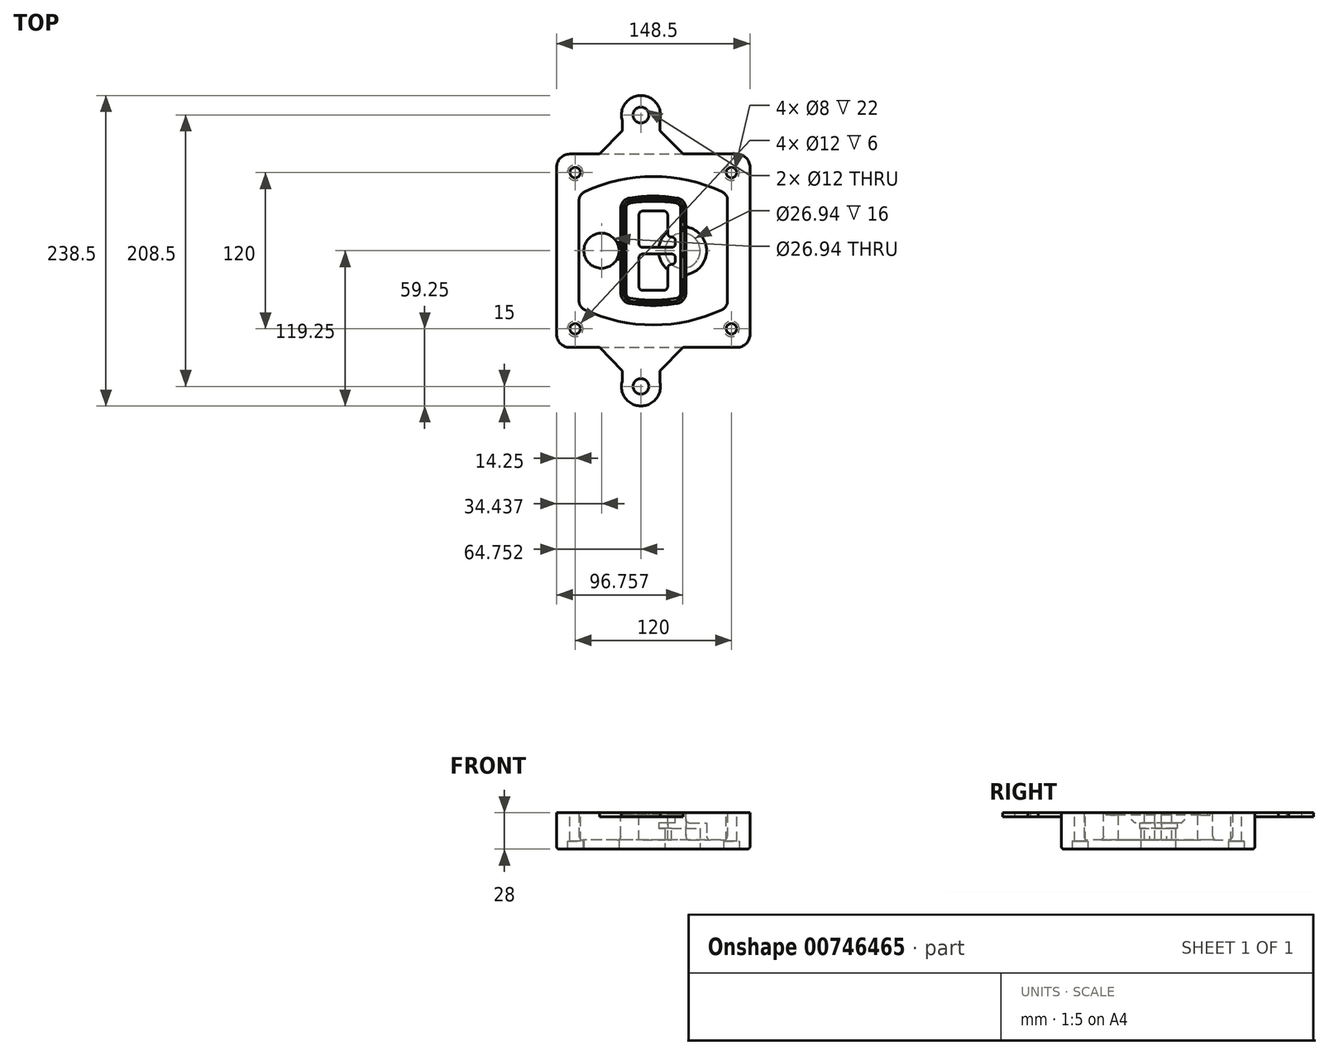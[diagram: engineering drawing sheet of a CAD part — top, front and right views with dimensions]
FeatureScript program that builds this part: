
annotation { "Feature Type Name" : "Feature", "Feature Type Description" : "" }
export const myFeature = defineFeature(function(context is Context, id is Id, definition is map)
    precondition{}
    {
        {
            var Q0;
            Q0=qCreatedBy(makeId("Top.planeOp"),FACE);
            var sketch = newSketch(context, id + "F0", { "sketchPlane" : qUnion([Q0])});
            skPoint(sketch, "E0.rect.middle", {"position": v(0, 0) * mm});
            skLineSegment(sketch, "E1.bottom", {"start": v(-64.25, -74.25) * mm, "end": v(64.25, -74.25) * mm});
            skLineSegment(sketch, "E1.top", {"start": v(-64.25, 74.25) * mm, "end": v(64.25, 74.25) * mm});
            skLineSegment(sketch, "E1.left", {"start": v(-74.25, -64.25) * mm, "end": v(-74.25, 64.25) * mm});
            skLineSegment(sketch, "E1.right", {"start": v(74.25, -64.25) * mm, "end": v(74.25, 64.25) * mm});
            skLineSegment(sketch, "E2", {"start": v(-74.25, 74.25) * mm, "end": v(74.25, -74.25) * mm, "construction": true});
            skLineSegment(sketch, "E3", {"start": v(74.25, 74.25) * mm, "end": v(-74.25, -74.25) * mm, "construction": true});
            skCircle(sketch, "E4", {"center": v(-60, 60) * mm, "radius": 4 * mm});
            skCircle(sketch, "E5", {"center": v(60, 60) * mm, "radius": 4 * mm});
            skCircle(sketch, "E6", {"center": v(60, -60) * mm, "radius": 4 * mm});
            skCircle(sketch, "E7", {"center": v(-60, -60) * mm, "radius": 4 * mm});
            skLineSegment(sketch, "E8", {"start": v(-60, 60) * mm, "end": v(60, 60) * mm, "construction": true});
            skLineSegment(sketch, "E9", {"start": v(60, 60) * mm, "end": v(60, -60) * mm, "construction": true});
            skLineSegment(sketch, "E10", {"start": v(60, -60) * mm, "end": v(-60, -60) * mm, "construction": true});
            skLineSegment(sketch, "E11", {"start": v(-60, -60) * mm, "end": v(-60, 60) * mm, "construction": true});
            skLineSegment(sketch, "E12", {"start": v(-60, 38.83) * mm, "end": v(-60, -38.83) * mm});
            skLineSegment(sketch, "E13", {"start": v(60, 38.83) * mm, "end": v(60, -38.83) * mm});
            skArc(sketch, "E14", {"start": v(54.26, 47.88) * mm, "mid": v(0, 60) * mm, "end": v(-54.26, 47.88) * mm});
            skArc(sketch, "E15", {"start": v(-54.26, -47.88) * mm, "mid": v(0, -60) * mm, "end": v(54.26, -47.88) * mm});
            skLineSegment(sketch, "E16", {"start": v(-60, 0) * mm, "end": v(60, 0) * mm, "construction": true});
            skPoint(sketch, "E17.visualSharp", {"position": v(-60, -45) * mm});
            skArc(sketch, "E17.filletArc", {"start": v(-60, -38.83) * mm, "mid": v(-58.44, -44.2) * mm, "end": v(-54.26, -47.88) * mm});
            skPoint(sketch, "E18.visualSharp", {"position": v(-60, 45) * mm});
            skArc(sketch, "E18.filletArc", {"start": v(-54.26, 47.88) * mm, "mid": v(-58.44, 44.2) * mm, "end": v(-60, 38.83) * mm});
            skPoint(sketch, "E19.visualSharp", {"position": v(60, 45) * mm});
            skArc(sketch, "E19.filletArc", {"start": v(60, 38.83) * mm, "mid": v(58.44, 44.2) * mm, "end": v(54.26, 47.88) * mm});
            skPoint(sketch, "E20.visualSharp", {"position": v(60, -45) * mm});
            skArc(sketch, "E20.filletArc", {"start": v(54.26, -47.88) * mm, "mid": v(58.44, -44.2) * mm, "end": v(60, -38.83) * mm});
            skPoint(sketch, "E21.visualSharp", {"position": v(-74.25, 74.25) * mm});
            skArc(sketch, "E21.filletArc", {"start": v(-64.25, 74.25) * mm, "mid": v(-71.32, 71.32) * mm, "end": v(-74.25, 64.25) * mm});
            skPoint(sketch, "E22.visualSharp", {"position": v(74.25, 74.25) * mm});
            skArc(sketch, "E22.filletArc", {"start": v(74.25, 64.25) * mm, "mid": v(71.32, 71.32) * mm, "end": v(64.25, 74.25) * mm});
            skPoint(sketch, "E23.visualSharp", {"position": v(74.25, -74.25) * mm});
            skArc(sketch, "E23.filletArc", {"start": v(64.25, -74.25) * mm, "mid": v(71.32, -71.32) * mm, "end": v(74.25, -64.25) * mm});
            skPoint(sketch, "E24.visualSharp", {"position": v(-74.25, -74.25) * mm});
            skArc(sketch, "E24.filletArc", {"start": v(-74.25, -64.25) * mm, "mid": v(-71.32, -71.32) * mm, "end": v(-64.25, -74.25) * mm});
            skArc(sketch, "E25.0", {"start": v(57, 38.83) * mm, "mid": v(55.9, 42.58) * mm, "end": v(52.98, 45.17) * mm});
            skLineSegment(sketch, "E25.1", {"start": v(57, 38.83) * mm, "end": v(57, -38.83) * mm});
            skArc(sketch, "E25.2", {"start": v(52.98, -45.17) * mm, "mid": v(55.9, -42.58) * mm, "end": v(57, -38.83) * mm});
            skArc(sketch, "E25.3", {"start": v(-52.98, -45.17) * mm, "mid": v(0, -57) * mm, "end": v(52.98, -45.17) * mm});
            skArc(sketch, "E25.4", {"start": v(-57, -38.83) * mm, "mid": v(-55.9, -42.58) * mm, "end": v(-52.98, -45.17) * mm});
            skArc(sketch, "E25.5", {"start": v(52.98, 45.17) * mm, "mid": v(0, 57) * mm, "end": v(-52.98, 45.17) * mm});
            skLineSegment(sketch, "E25.6", {"start": v(-57, 38.83) * mm, "end": v(-57, -38.83) * mm});
            skArc(sketch, "E25.7", {"start": v(-52.98, 45.17) * mm, "mid": v(-55.9, 42.58) * mm, "end": v(-57, 38.83) * mm});
            skArc(sketch, "E26.0", {"start": v(-55.96, 51.5) * mm, "mid": v(-61.82, 46.33) * mm, "end": v(-64, 38.83) * mm});
            skArc(sketch, "E26.1", {"start": v(55.96, 51.5) * mm, "mid": v(0, 64) * mm, "end": v(-55.96, 51.5) * mm});
            skArc(sketch, "E26.2", {"start": v(64, 38.83) * mm, "mid": v(61.82, 46.33) * mm, "end": v(55.96, 51.5) * mm});
            skLineSegment(sketch, "E26.3", {"start": v(64, 38.83) * mm, "end": v(64, -38.83) * mm});
            skArc(sketch, "E26.4", {"start": v(55.96, -51.5) * mm, "mid": v(61.82, -46.33) * mm, "end": v(64, -38.83) * mm});
            skLineSegment(sketch, "E26.5", {"start": v(-64, 38.83) * mm, "end": v(-64, -38.83) * mm});
            skArc(sketch, "E26.6", {"start": v(-55.96, -51.5) * mm, "mid": v(0, -64) * mm, "end": v(55.96, -51.5) * mm});
            skArc(sketch, "E26.7", {"start": v(-64, -38.83) * mm, "mid": v(-61.82, -46.33) * mm, "end": v(-55.96, -51.5) * mm});
            skSolve(sketch);
        }
        {
            var Q0;
            Q0=makeQuery(id+"F0.imprint","IMPRINT",FACE,{"disambiguationData":[TD([[makeQuery(id+"F0.imprint","IMPRINT",EDGE,{"derivedFrom":sQuery(id+"F0.wireOp",EDGE,"E1.bottom")}),1.0]])]});
            var Q1;
            Q1=makeQuery(id+"F0.imprint","IMPRINT",FACE,{"disambiguationData":[TD([[makeQuery(id+"F0.imprint","IMPRINT",EDGE,{"derivedFrom":sQuery(id+"F0.wireOp",EDGE,"E12")}),1.0]])]});
            var Q2;
            Q2=makeQuery(id+"F0.imprint","IMPRINT",FACE,{"disambiguationData":[TD([[makeQuery(id+"F0.imprint","IMPRINT",EDGE,{"derivedFrom":sQuery(id+"F0.wireOp",EDGE,"E25.0")}),1.0]])]});
            var Q3;
            Q3=makeQuery(id+"F0.imprint","IMPRINT",FACE,{"disambiguationData":[TD([[makeQuery(id+"F0.imprint","IMPRINT",EDGE,{"derivedFrom":sQuery(id+"F0.wireOp",EDGE,"E12")}),-1.0]])]});
            extrude(context, id + "F1", {"entities" : qUnion([Q0, Q1, Q2, Q3]), "oppositeDirection" : true, "depth" : 25 * mm});
        }
        {
            var Q0;
            Q0=makeQuery(id+"F0.imprint","IMPRINT",FACE,{"disambiguationData":[TD([[makeQuery(id+"F0.imprint","IMPRINT",EDGE,{"derivedFrom":sQuery(id+"F0.wireOp",EDGE,"E12")}),1.0]])]});
            extrude(context, id + "F2", {"entities" : qUnion([Q0]), "operationType" : NewBodyOperationType.ADD, "depth" : 3 * mm});
        }
        {
            var Q0;
            Q0=makeQuery(id+"F0.imprint","IMPRINT",FACE,{"disambiguationData":[TD([[makeQuery(id+"F0.imprint","IMPRINT",EDGE,{"derivedFrom":sQuery(id+"F0.wireOp",EDGE,"E25.0")}),1.0]])]});
            extrude(context, id + "F3", {"entities" : qUnion([Q0]), "operationType" : NewBodyOperationType.REMOVE, "oppositeDirection" : true, "depth" : 18 * mm});
        }
        {
            var Q0;
            Q0=makeQuery(id+"F2.opExtrude","CAP_FACE",FACE,{"disambiguationData":[OSD([sQuery(id+"F0.wireOp",EDGE,"E12"),sQuery(id+"F0.wireOp",EDGE,"E13"),sQuery(id+"F0.wireOp",EDGE,"E14"),sQuery(id+"F0.wireOp",EDGE,"E15"),sQuery(id+"F0.wireOp",EDGE,"E17.filletArc"),sQuery(id+"F0.wireOp",EDGE,"E18.filletArc"),sQuery(id+"F0.wireOp",EDGE,"E19.filletArc"),sQuery(id+"F0.wireOp",EDGE,"E20.filletArc"),sQuery(id+"F0.wireOp",EDGE,"E25.0"),sQuery(id+"F0.wireOp",EDGE,"E25.1"),sQuery(id+"F0.wireOp",EDGE,"E25.2"),sQuery(id+"F0.wireOp",EDGE,"E25.3"),sQuery(id+"F0.wireOp",EDGE,"E25.4"),sQuery(id+"F0.wireOp",EDGE,"E25.5"),sQuery(id+"F0.wireOp",EDGE,"E25.6"),sQuery(id+"F0.wireOp",EDGE,"E25.7")])],"isStart":false});
            var sketch = newSketch(context, id + "F4", { "sketchPlane" : qUnion([Q0])});
            skArc(sketch, "E27.0", {"start": v(-18.34, -40.45) * mm, "mid": v(0, -42) * mm, "end": v(18.34, -40.45) * mm});
            skArc(sketch, "E28.0", {"start": v(18.34, 40.45) * mm, "mid": v(0, 42) * mm, "end": v(-18.34, 40.45) * mm});
            skLineSegment(sketch, "E29", {"start": v(-25, 32.57) * mm, "end": v(-25, -32.57) * mm});
            skLineSegment(sketch, "E30", {"start": v(25, 32.57) * mm, "end": v(25, -32.57) * mm});
            skLineSegment(sketch, "E31", {"start": v(-25, 39.1) * mm, "end": v(25, 39.1) * mm, "construction": true});
            skLineSegment(sketch, "E32", {"start": v(-25, -39.1) * mm, "end": v(25, -39.1) * mm, "construction": true});
            skPoint(sketch, "E33.visualSharp", {"position": v(-25, 39.1) * mm});
            skArc(sketch, "E33.filletArc", {"start": v(-18.34, 40.45) * mm, "mid": v(-23.11, 37.73) * mm, "end": v(-25, 32.57) * mm});
            skPoint(sketch, "E34.visualSharp", {"position": v(25, 39.1) * mm});
            skArc(sketch, "E34.filletArc", {"start": v(25, 32.57) * mm, "mid": v(23.11, 37.73) * mm, "end": v(18.34, 40.45) * mm});
            skPoint(sketch, "E35.visualSharp", {"position": v(25, -39.1) * mm});
            skArc(sketch, "E35.filletArc", {"start": v(18.34, -40.45) * mm, "mid": v(23.11, -37.73) * mm, "end": v(25, -32.57) * mm});
            skPoint(sketch, "E36.visualSharp", {"position": v(-25, -39.1) * mm});
            skArc(sketch, "E36.filletArc", {"start": v(-25, -32.57) * mm, "mid": v(-23.11, -37.73) * mm, "end": v(-18.34, -40.45) * mm});
            skArc(sketch, "E37.0", {"start": v(52.98, 45.17) * mm, "mid": v(0, 57) * mm, "end": v(-52.98, 45.17) * mm});
            skArc(sketch, "E37.1", {"start": v(-52.98, 45.17) * mm, "mid": v(-55.9, 42.58) * mm, "end": v(-57, 38.83) * mm});
            skLineSegment(sketch, "E37.2", {"start": v(-57, 38.83) * mm, "end": v(-57, -38.83) * mm});
            skArc(sketch, "E37.3", {"start": v(-57, -38.83) * mm, "mid": v(-55.9, -42.58) * mm, "end": v(-52.98, -45.17) * mm});
            skArc(sketch, "E37.4", {"start": v(-52.98, -45.17) * mm, "mid": v(0, -57) * mm, "end": v(52.98, -45.17) * mm});
            skArc(sketch, "E37.5", {"start": v(52.98, -45.17) * mm, "mid": v(55.9, -42.58) * mm, "end": v(57, -38.83) * mm});
            skLineSegment(sketch, "E37.6", {"start": v(57, 38.83) * mm, "end": v(57, -38.83) * mm});
            skArc(sketch, "E37.7", {"start": v(57, 38.83) * mm, "mid": v(55.9, 42.58) * mm, "end": v(52.98, 45.17) * mm});
            skLineSegment(sketch, "E38.0", {"start": v(23, 32.57) * mm, "end": v(23, -32.57) * mm});
            skArc(sketch, "E38.1", {"start": v(18, -38.48) * mm, "mid": v(21.58, -36.44) * mm, "end": v(23, -32.57) * mm});
            skArc(sketch, "E38.2", {"start": v(-18, -38.48) * mm, "mid": v(0, -40) * mm, "end": v(18, -38.48) * mm});
            skArc(sketch, "E38.3", {"start": v(-23, -32.57) * mm, "mid": v(-21.58, -36.44) * mm, "end": v(-18, -38.48) * mm});
            skLineSegment(sketch, "E38.4", {"start": v(-23, 32.57) * mm, "end": v(-23, -32.57) * mm});
            skArc(sketch, "E38.5", {"start": v(23, 32.57) * mm, "mid": v(21.58, 36.44) * mm, "end": v(18, 38.48) * mm});
            skArc(sketch, "E38.6", {"start": v(-18, 38.48) * mm, "mid": v(-21.58, 36.44) * mm, "end": v(-23, 32.57) * mm});
            skArc(sketch, "E38.7", {"start": v(18, 38.48) * mm, "mid": v(0, 40) * mm, "end": v(-18, 38.48) * mm});
            skArc(sketch, "E39.0", {"start": v(21, 32.57) * mm, "mid": v(20.06, 35.15) * mm, "end": v(17.67, 36.5) * mm});
            skLineSegment(sketch, "E39.1", {"start": v(21, 32.57) * mm, "end": v(21, -32.57) * mm});
            skArc(sketch, "E39.2", {"start": v(17.67, -36.5) * mm, "mid": v(20.06, -35.15) * mm, "end": v(21, -32.57) * mm});
            skArc(sketch, "E39.3", {"start": v(-17.67, -36.5) * mm, "mid": v(0, -38) * mm, "end": v(17.67, -36.5) * mm});
            skArc(sketch, "E39.4", {"start": v(-21, -32.57) * mm, "mid": v(-20.06, -35.15) * mm, "end": v(-17.67, -36.5) * mm});
            skArc(sketch, "E39.5", {"start": v(17.67, 36.5) * mm, "mid": v(0, 38) * mm, "end": v(-17.67, 36.5) * mm});
            skLineSegment(sketch, "E39.6", {"start": v(-21, 32.57) * mm, "end": v(-21, -32.57) * mm});
            skArc(sketch, "E39.7", {"start": v(-17.67, 36.5) * mm, "mid": v(-20.06, 35.15) * mm, "end": v(-21, 32.57) * mm});
            skLineSegment(sketch, "E40", {"start": v(-25, 0) * mm, "end": v(25, 0) * mm, "construction": true});
            skLineSegment(sketch, "E41", {"start": v(-11, 5.5) * mm, "end": v(-11, 27.5) * mm});
            skLineSegment(sketch, "E42", {"start": v(-8, 30.5) * mm, "end": v(8, 30.5) * mm});
            skLineSegment(sketch, "E43", {"start": v(11, 27.5) * mm, "end": v(11, 13.5) * mm});
            skLineSegment(sketch, "E44", {"start": v(14, 10.5) * mm, "end": v(14, 10.5) * mm});
            skLineSegment(sketch, "E45", {"start": v(17, 7.5) * mm, "end": v(17, 5.5) * mm});
            skLineSegment(sketch, "E46", {"start": v(14, 2.5) * mm, "end": v(-8, 2.5) * mm});
            skPoint(sketch, "E47.visualSharp", {"position": v(-11, 30.5) * mm});
            skArc(sketch, "E47.filletArc", {"start": v(-8, 30.5) * mm, "mid": v(-10.12, 29.62) * mm, "end": v(-11, 27.5) * mm});
            skPoint(sketch, "E48.visualSharp", {"position": v(11, 30.5) * mm});
            skArc(sketch, "E48.filletArc", {"start": v(11, 27.5) * mm, "mid": v(10.12, 29.62) * mm, "end": v(8, 30.5) * mm});
            skPoint(sketch, "E49.visualSharp", {"position": v(11, 10.5) * mm});
            skArc(sketch, "E49.filletArc", {"start": v(11, 13.5) * mm, "mid": v(11.88, 11.38) * mm, "end": v(14, 10.5) * mm});
            skPoint(sketch, "E50.visualSharp", {"position": v(17, 10.5) * mm});
            skArc(sketch, "E50.filletArc", {"start": v(17, 7.5) * mm, "mid": v(16.12, 9.62) * mm, "end": v(14, 10.5) * mm});
            skPoint(sketch, "E51.visualSharp", {"position": v(17, 2.5) * mm});
            skArc(sketch, "E51.filletArc", {"start": v(14, 2.5) * mm, "mid": v(16.12, 3.38) * mm, "end": v(17, 5.5) * mm});
            skPoint(sketch, "E52.visualSharp", {"position": v(-11, 2.5) * mm});
            skArc(sketch, "E52.filletArc", {"start": v(-11, 5.5) * mm, "mid": v(-10.12, 3.38) * mm, "end": v(-8, 2.5) * mm});
            skLineSegment(sketch, "E53.0.MirrorCS", {"start": v(14, -2.5) * mm, "end": v(-8, -2.5) * mm});
            skArc(sketch, "E54.0.MirrorCS", {"start": v(-11, -5.5) * mm, "mid": v(-10.12, -3.38) * mm, "end": v(-8, -2.5) * mm});
            skLineSegment(sketch, "E55.0.MirrorCS", {"start": v(-11, -5.5) * mm, "end": v(-11, -27.5) * mm});
            skArc(sketch, "E56.0.MirrorCS", {"start": v(-8, -30.5) * mm, "mid": v(-10.12, -29.62) * mm, "end": v(-11, -27.5) * mm});
            skLineSegment(sketch, "E57.0.MirrorCS", {"start": v(-8, -30.5) * mm, "end": v(8, -30.5) * mm});
            skArc(sketch, "E58.0.MirrorCS", {"start": v(11, -27.5) * mm, "mid": v(10.12, -29.62) * mm, "end": v(8, -30.5) * mm});
            skLineSegment(sketch, "E59.0.MirrorCS", {"start": v(11, -27.5) * mm, "end": v(11, -13.5) * mm});
            skArc(sketch, "E60.0.MirrorCS", {"start": v(11, -13.5) * mm, "mid": v(11.88, -11.38) * mm, "end": v(14, -10.5) * mm});
            skArc(sketch, "E61.0.MirrorCS", {"start": v(17, -7.5) * mm, "mid": v(16.12, -9.62) * mm, "end": v(14, -10.5) * mm});
            skLineSegment(sketch, "E62.0.MirrorCS", {"start": v(17, -7.5) * mm, "end": v(17, -5.5) * mm});
            skArc(sketch, "E63.0.MirrorCS", {"start": v(14, -2.5) * mm, "mid": v(16.12, -3.38) * mm, "end": v(17, -5.5) * mm});
            skSolve(sketch);
        }
        {
            var Q0;
            Q0=makeQuery(id+"F4.imprint","IMPRINT",FACE,{"disambiguationData":[TD([[makeQuery(id+"F4.imprint","IMPRINT",EDGE,{"derivedFrom":sQuery(id+"F4.wireOp",EDGE,"E27.0")}),1.0]])]});
            var Q1;
            Q1=makeQuery(id+"F4.imprint","IMPRINT",FACE,{"disambiguationData":[TD([[makeQuery(id+"F4.imprint","IMPRINT",EDGE,{"derivedFrom":sQuery(id+"F4.wireOp",EDGE,"E38.0")}),-1.0]])]});
            var Q2;
            Q2=makeQuery(id+"F4.imprint","IMPRINT",FACE,{"disambiguationData":[TD([[makeQuery(id+"F4.imprint","IMPRINT",EDGE,{"derivedFrom":sQuery(id+"F4.wireOp",EDGE,"E39.0")}),1.0]])]});
            extrude(context, id + "F5", {"entities" : qUnion([Q0, Q1, Q2]), "operationType" : NewBodyOperationType.ADD, "endBound" : BoundingType.UP_TO_NEXT, "oppositeDirection" : true, "depth" : 25 * mm});
        }
        {
            var Q0;
            Q0=makeQuery(id+"F4.imprint","IMPRINT",FACE,{"disambiguationData":[TD([[makeQuery(id+"F4.imprint","IMPRINT",EDGE,{"derivedFrom":sQuery(id+"F4.wireOp",EDGE,"E38.0")}),-1.0]])]});
            extrude(context, id + "F6", {"entities" : qUnion([Q0]), "operationType" : NewBodyOperationType.REMOVE, "oppositeDirection" : true, "depth" : 2 * mm});
        }
        {
            var Q0;
            Q0=makeQuery(id+"F1.opExtrude","CAP_FACE",FACE,{"disambiguationData":[OSD([sQuery(id+"F0.wireOp",EDGE,"E1.bottom"),sQuery(id+"F0.wireOp",EDGE,"E1.top"),sQuery(id+"F0.wireOp",EDGE,"E1.left"),sQuery(id+"F0.wireOp",EDGE,"E1.right"),sQuery(id+"F0.wireOp",EDGE,"E4"),sQuery(id+"F0.wireOp",EDGE,"E5"),sQuery(id+"F0.wireOp",EDGE,"E6"),sQuery(id+"F0.wireOp",EDGE,"E7"),sQuery(id+"F0.wireOp",EDGE,"E21.filletArc"),sQuery(id+"F0.wireOp",EDGE,"E22.filletArc"),sQuery(id+"F0.wireOp",EDGE,"E23.filletArc"),sQuery(id+"F0.wireOp",EDGE,"E24.filletArc")])],"isStart":false});
            var sketch = newSketch(context, id + "F7", { "sketchPlane" : qUnion([Q0])});
            skCircle(sketch, "E64", {"center": v(22.5, 0) * mm, "radius": 13.47 * mm});
            skCircle(sketch, "E65", {"center": v(-39.81, 0) * mm, "radius": 13.47 * mm});
            skLineSegment(sketch, "E66", {"start": v(74.25, 0) * mm, "end": v(-74.25, 0) * mm});
            skCircle(sketch, "E67", {"center": v(22.5, 0) * mm, "radius": 18.47 * mm});
            skCircle(sketch, "E68", {"center": v(60, -60) * mm, "radius": 6 * mm});
            skCircle(sketch, "E69", {"center": v(-60, -60) * mm, "radius": 6 * mm});
            skCircle(sketch, "E70", {"center": v(-60, 60) * mm, "radius": 6 * mm});
            skCircle(sketch, "E71", {"center": v(60, 60) * mm, "radius": 6 * mm});
            skSolve(sketch);
        }
        {
            var Q0;
            {var subQ1=sQuery(id+"F7.wireOp",EDGE,"E66");var subQ4=sQuery(id+"F7.wireOp",EDGE,"E64");var subQ6=makeQuery(id+"F7.imprint","INTERSECT",VERTEX,{"disambiguationData":[OD(0.0)],"derivedFrom":[subQ4,subQ1]});Q0=makeQuery(id+"F7.imprint","IMPRINT",FACE,{"disambiguationData":[TD([[makeQuery(id+"F7.imprint","IMPRINT",EDGE,{"disambiguationData":[TD([[subQ6,-1.0]])],"derivedFrom":subQ4}),-1.0]])]});}
            var Q1;
            {var subQ0=sQuery(id+"F7.wireOp",EDGE,"E66");var subQ1=sQuery(id+"F7.wireOp",EDGE,"E64");var subQ3=makeQuery(id+"F7.imprint","INTERSECT",VERTEX,{"disambiguationData":[OD(0.0)],"derivedFrom":[subQ1,subQ0]});Q1=makeQuery(id+"F7.imprint","IMPRINT",FACE,{"disambiguationData":[TD([[makeQuery(id+"F7.imprint","IMPRINT",EDGE,{"disambiguationData":[TD([[subQ3,-1.0]])],"derivedFrom":subQ1}),1.0]])]});}
            var Q2;
            {var subQ0=sQuery(id+"F7.wireOp",EDGE,"E66");var subQ1=sQuery(id+"F7.wireOp",EDGE,"E64");var subQ3=makeQuery(id+"F7.imprint","INTERSECT",VERTEX,{"disambiguationData":[OD(0.0)],"derivedFrom":[subQ1,subQ0]});Q2=makeQuery(id+"F7.imprint","IMPRINT",FACE,{"disambiguationData":[TD([[makeQuery(id+"F7.imprint","IMPRINT",EDGE,{"disambiguationData":[TD([[subQ3,1.0]])],"derivedFrom":subQ1}),1.0]])]});}
            var Q3;
            {var subQ1=sQuery(id+"F7.wireOp",EDGE,"E66");var subQ4=sQuery(id+"F7.wireOp",EDGE,"E64");var subQ6=makeQuery(id+"F7.imprint","INTERSECT",VERTEX,{"disambiguationData":[OD(0.0)],"derivedFrom":[subQ4,subQ1]});Q3=makeQuery(id+"F7.imprint","IMPRINT",FACE,{"disambiguationData":[TD([[makeQuery(id+"F7.imprint","IMPRINT",EDGE,{"disambiguationData":[TD([[subQ6,1.0]])],"derivedFrom":subQ4}),-1.0]])]});}
            extrude(context, id + "F8", {"entities" : qUnion([Q0, Q1, Q2, Q3]), "operationType" : NewBodyOperationType.ADD, "oppositeDirection" : true, "depth" : 20 * mm});
        }
        {
            var Q0;
            {var subQ0=sQuery(id+"F7.wireOp",EDGE,"E66");var subQ1=sQuery(id+"F7.wireOp",EDGE,"E64");var subQ3=makeQuery(id+"F7.imprint","INTERSECT",VERTEX,{"disambiguationData":[OD(0.0)],"derivedFrom":[subQ1,subQ0]});Q0=makeQuery(id+"F7.imprint","IMPRINT",FACE,{"disambiguationData":[TD([[makeQuery(id+"F7.imprint","IMPRINT",EDGE,{"disambiguationData":[TD([[subQ3,-1.0]])],"derivedFrom":subQ1}),1.0]])]});}
            var Q1;
            {var subQ0=sQuery(id+"F7.wireOp",EDGE,"E66");var subQ1=sQuery(id+"F7.wireOp",EDGE,"E64");var subQ3=makeQuery(id+"F7.imprint","INTERSECT",VERTEX,{"disambiguationData":[OD(0.0)],"derivedFrom":[subQ1,subQ0]});Q1=makeQuery(id+"F7.imprint","IMPRINT",FACE,{"disambiguationData":[TD([[makeQuery(id+"F7.imprint","IMPRINT",EDGE,{"disambiguationData":[TD([[subQ3,1.0]])],"derivedFrom":subQ1}),1.0]])]});}
            extrude(context, id + "F9", {"entities" : qUnion([Q0, Q1]), "operationType" : NewBodyOperationType.REMOVE, "oppositeDirection" : true, "depth" : 16 * mm});
        }
        {
            var Q0;
            {var subQ0=sQuery(id+"F7.wireOp",EDGE,"E66");var subQ1=sQuery(id+"F7.wireOp",EDGE,"E65");var subQ3=makeQuery(id+"F7.imprint","INTERSECT",VERTEX,{"disambiguationData":[OD(0.0)],"derivedFrom":[subQ1,subQ0]});Q0=makeQuery(id+"F7.imprint","IMPRINT",FACE,{"disambiguationData":[TD([[makeQuery(id+"F7.imprint","IMPRINT",EDGE,{"disambiguationData":[TD([[subQ3,-1.0]])],"derivedFrom":subQ1}),1.0]])]});}
            var Q1;
            {var subQ0=sQuery(id+"F7.wireOp",EDGE,"E66");var subQ1=sQuery(id+"F7.wireOp",EDGE,"E65");var subQ3=makeQuery(id+"F7.imprint","INTERSECT",VERTEX,{"disambiguationData":[OD(0.0)],"derivedFrom":[subQ1,subQ0]});Q1=makeQuery(id+"F7.imprint","IMPRINT",FACE,{"disambiguationData":[TD([[makeQuery(id+"F7.imprint","IMPRINT",EDGE,{"disambiguationData":[TD([[subQ3,1.0]])],"derivedFrom":subQ1}),1.0]])]});}
            extrude(context, id + "F10", {"entities" : qUnion([Q0, Q1]), "operationType" : NewBodyOperationType.REMOVE, "oppositeDirection" : true, "depth" : 25 * mm});
        }
        {
            var Q0;
            Q0=makeQuery(id+"F7.imprint","IMPRINT",FACE,{"disambiguationData":[TD([[makeQuery(id+"F7.imprint","IMPRINT",EDGE,{"derivedFrom":sQuery(id+"F7.wireOp",EDGE,"E68")}),1.0]])]});
            var Q1;
            Q1=makeQuery(id+"F7.imprint","IMPRINT",FACE,{"disambiguationData":[TD([[makeQuery(id+"F7.imprint","IMPRINT",EDGE,{"derivedFrom":makeQuery(id+"F1.opExtrude","CAP_EDGE",EDGE,{"disambiguationData":[OSD([sQuery(id+"F0.wireOp",EDGE,"E5")])],"isStart":false})}),-1.0]])]});
            var Q2;
            Q2=makeQuery(id+"F7.imprint","IMPRINT",FACE,{"disambiguationData":[TD([[makeQuery(id+"F7.imprint","IMPRINT",EDGE,{"derivedFrom":sQuery(id+"F7.wireOp",EDGE,"E69")}),1.0]])]});
            var Q3;
            Q3=makeQuery(id+"F7.imprint","IMPRINT",FACE,{"disambiguationData":[TD([[makeQuery(id+"F7.imprint","IMPRINT",EDGE,{"derivedFrom":makeQuery(id+"F1.opExtrude","CAP_EDGE",EDGE,{"disambiguationData":[OSD([sQuery(id+"F0.wireOp",EDGE,"E4")])],"isStart":false})}),-1.0]])]});
            var Q4;
            Q4=makeQuery(id+"F7.imprint","IMPRINT",FACE,{"disambiguationData":[TD([[makeQuery(id+"F7.imprint","IMPRINT",EDGE,{"derivedFrom":sQuery(id+"F7.wireOp",EDGE,"E70")}),1.0]])]});
            var Q5;
            Q5=makeQuery(id+"F7.imprint","IMPRINT",FACE,{"disambiguationData":[TD([[makeQuery(id+"F7.imprint","IMPRINT",EDGE,{"derivedFrom":makeQuery(id+"F1.opExtrude","CAP_EDGE",EDGE,{"disambiguationData":[OSD([sQuery(id+"F0.wireOp",EDGE,"E7")])],"isStart":false})}),-1.0]])]});
            var Q6;
            Q6=makeQuery(id+"F7.imprint","IMPRINT",FACE,{"disambiguationData":[TD([[makeQuery(id+"F7.imprint","IMPRINT",EDGE,{"derivedFrom":sQuery(id+"F7.wireOp",EDGE,"E71")}),1.0]])]});
            var Q7;
            Q7=makeQuery(id+"F7.imprint","IMPRINT",FACE,{"disambiguationData":[TD([[makeQuery(id+"F7.imprint","IMPRINT",EDGE,{"derivedFrom":makeQuery(id+"F1.opExtrude","CAP_EDGE",EDGE,{"disambiguationData":[OSD([sQuery(id+"F0.wireOp",EDGE,"E6")])],"isStart":false})}),-1.0]])]});
            extrude(context, id + "F11", {"entities" : qUnion([Q0, Q1, Q2, Q3, Q4, Q5, Q6, Q7]), "operationType" : NewBodyOperationType.REMOVE, "oppositeDirection" : true, "depth" : 6 * mm});
        }
        {
            var Q0;
            Q0=makeQuery(id+"F9.boolean.opBoolean","COPY",FACE,{"derivedFrom":makeQuery(id+"F9.opExtrude","CAP_FACE",FACE,{"disambiguationData":[OSD([sQuery(id+"F7.wireOp",EDGE,"E64")])],"isStart":false})});
            var sketch = newSketch(context, id + "F12", { "sketchPlane" : qUnion([Q0])});
            skArc(sketch, "E72.0", {"start": v(11, 14.45) * mm, "mid": v(6.45, 9.13) * mm, "end": v(4.2, 2.5) * mm});
            skArc(sketch, "E72.1", {"start": v(4.2, -2.5) * mm, "mid": v(6.45, -9.13) * mm, "end": v(11, -14.45) * mm});
            skLineSegment(sketch, "E73", {"start": v(4.2, -2.5) * mm, "end": v(14, -2.5) * mm});
            skLineSegment(sketch, "E74.0", {"start": v(14, 2.5) * mm, "end": v(4.2, 2.5) * mm});
            skArc(sketch, "E74.1", {"start": v(14, 2.5) * mm, "mid": v(16.12, 3.38) * mm, "end": v(17, 5.5) * mm});
            skLineSegment(sketch, "E74.2", {"start": v(17, 7.5) * mm, "end": v(17, 5.5) * mm});
            skArc(sketch, "E74.3", {"start": v(17, 7.5) * mm, "mid": v(16.12, 9.62) * mm, "end": v(14, 10.5) * mm});
            skArc(sketch, "E74.4", {"start": v(11, 13.5) * mm, "mid": v(11.88, 11.38) * mm, "end": v(14, 10.5) * mm});
            skLineSegment(sketch, "E74.5", {"start": v(11, 14.45) * mm, "end": v(11, 13.5) * mm});
            skLineSegment(sketch, "E74.7", {"start": v(14, -2.5) * mm, "end": v(4.2, -2.5) * mm});
            skArc(sketch, "E74.8", {"start": v(14, -2.5) * mm, "mid": v(16.12, -3.38) * mm, "end": v(17, -5.5) * mm});
            skLineSegment(sketch, "E74.9", {"start": v(17, -7.5) * mm, "end": v(17, -5.5) * mm});
            skArc(sketch, "E74.10", {"start": v(17, -7.5) * mm, "mid": v(16.12, -9.62) * mm, "end": v(14, -10.5) * mm});
            skArc(sketch, "E74.11", {"start": v(11, -13.5) * mm, "mid": v(11.88, -11.38) * mm, "end": v(14, -10.5) * mm});
            skLineSegment(sketch, "E74.12", {"start": v(11, -14.45) * mm, "end": v(11, -13.5) * mm});
            skPoint(sketch, "E75.orphan", {"position": v(11, -27.5) * mm});
            skPoint(sketch, "E76.orphan", {"position": v(-8, -2.5) * mm});
            skPoint(sketch, "E77.orphan", {"position": v(-8, 2.5) * mm});
            skPoint(sketch, "E78.orphan", {"position": v(11, 27.5) * mm});
            skSolve(sketch);
        }
        {
            var Q0;
            {var subQ7=sQuery(id+"F12.wireOp",EDGE,"E72.0");var subQ14=sQuery(id+"F12.wireOp",EDGE,"E72.1");var subQ16=sQuery(id+"F12.wireOp",EDGE,"E74.1");var subQ18=sQuery(id+"F12.wireOp",EDGE,"E74.8");Q0=qUnion([makeQuery(id+"F12.imprint","IMPRINT",FACE,{"disambiguationData":[TD([[makeQuery(id+"F12.imprint","IMPRINT",EDGE,{"derivedFrom":subQ7}),1.0]])]}),makeQuery(id+"F12.imprint","IMPRINT",FACE,{"disambiguationData":[TD([[makeQuery(id+"F12.imprint","IMPRINT",EDGE,{"derivedFrom":subQ14}),1.0]])]}),makeQuery(id+"F12.imprint","IMPRINT",FACE,{"disambiguationData":[TD([[makeQuery(id+"F12.imprint","IMPRINT",EDGE,{"derivedFrom":subQ16}),1.0]])]}),makeQuery(id+"F12.imprint","IMPRINT",FACE,{"disambiguationData":[TD([[makeQuery(id+"F12.imprint","IMPRINT",EDGE,{"derivedFrom":subQ18}),-1.0]])]})]);}
            var Q1;
            Q1=makeQuery(id+"F5.boolean.opBoolean","SPLIT",FACE,{"disambiguationData":[TD([makeQuery(id+"F5.opExtrude","SWEPT_FACE",FACE,{"disambiguationData":[OSD([sQuery(id+"F4.wireOp",EDGE,"E41")])]})])],"derivedFrom":makeQuery(id+"F3.boolean.opBoolean","COPY",FACE,{"derivedFrom":makeQuery(id+"F3.opExtrude","CAP_FACE",FACE,{"disambiguationData":[OSD([sQuery(id+"F0.wireOp",EDGE,"E25.0"),sQuery(id+"F0.wireOp",EDGE,"E25.1"),sQuery(id+"F0.wireOp",EDGE,"E25.2"),sQuery(id+"F0.wireOp",EDGE,"E25.3"),sQuery(id+"F0.wireOp",EDGE,"E25.4"),sQuery(id+"F0.wireOp",EDGE,"E25.5"),sQuery(id+"F0.wireOp",EDGE,"E25.6"),sQuery(id+"F0.wireOp",EDGE,"E25.7")])],"isStart":false})})});
            extrude(context, id + "F13", {"entities" : qUnion([Q0]), "operationType" : NewBodyOperationType.REMOVE, "endBound" : BoundingType.UP_TO_SURFACE, "endBoundEntityFace" : qUnion([Q1]), "depth" : 25 * mm});
        }
        {
            var Q0;
            Q0=makeQuery(id+"F3.boolean.opBoolean","COPY",EDGE,{"derivedFrom":makeQuery(id+"F3.opExtrude","CAP_EDGE",EDGE,{"disambiguationData":[OSD([sQuery(id+"F0.wireOp",EDGE,"E25.6")])],"isStart":false})});
            var Q1;
            Q1=makeQuery(id+"F8.boolean.opBoolean","INTERSECT",EDGE,{"derivedFrom":[makeQuery(id+"F5.opExtrude","SWEPT_FACE",FACE,{"disambiguationData":[OSD([sQuery(id+"F4.wireOp",EDGE,"E30")])]}),makeQuery(id+"F8.opExtrude","CAP_FACE",FACE,{"disambiguationData":[OSD([sQuery(id+"F7.wireOp",EDGE,"E67")])],"isStart":false})]});
            var Q2;
            Q2=makeQuery(id+"F8.boolean.opBoolean","INTERSECT",EDGE,{"disambiguationData":[OD(1.0)],"derivedFrom":[makeQuery(id+"F5.opExtrude","SWEPT_FACE",FACE,{"disambiguationData":[OSD([sQuery(id+"F4.wireOp",EDGE,"E30")])]}),makeQuery(id+"F8.opExtrude","SWEPT_FACE",FACE,{"disambiguationData":[OSD([sQuery(id+"F7.wireOp",EDGE,"E67")])]})]});
            var Q3;
            {var subQ0=sQuery(id+"F4.wireOp",EDGE,"E30");Q3=makeQuery(id+"F8.boolean.opBoolean","SPLIT",EDGE,{"disambiguationData":[TD([makeQuery(id+"F5.opExtrude","SWEPT_FACE",FACE,{"disambiguationData":[OSD([sQuery(id+"F4.wireOp",EDGE,"E35.filletArc")])]})])],"derivedFrom":makeQuery(id+"F5.opExtrude","CAP_EDGE",EDGE,{"disambiguationData":[OSD([subQ0])],"isStart":false})});}
            var Q4;
            {var subQ0=sQuery(id+"F0.wireOp",EDGE,"E25.7");var subQ1=sQuery(id+"F0.wireOp",EDGE,"E25.1");var subQ2=sQuery(id+"F0.wireOp",EDGE,"E25.6");var subQ3=sQuery(id+"F0.wireOp",EDGE,"E25.5");var subQ4=sQuery(id+"F0.wireOp",EDGE,"E25.4");var subQ5=sQuery(id+"F0.wireOp",EDGE,"E25.0");var subQ6=sQuery(id+"F0.wireOp",EDGE,"E25.2");var subQ7=sQuery(id+"F0.wireOp",EDGE,"E25.3");Q4=makeQuery(id+"F8.boolean.opBoolean","INTERSECT",EDGE,{"derivedFrom":[makeQuery(id+"F5.boolean.opBoolean","SPLIT",FACE,{"disambiguationData":[TD([makeQuery(id+"F2.opExtrude","SWEPT_FACE",FACE,{"disambiguationData":[OSD([subQ5])]})])],"derivedFrom":makeQuery(id+"F3.boolean.opBoolean","COPY",FACE,{"derivedFrom":makeQuery(id+"F3.opExtrude","CAP_FACE",FACE,{"disambiguationData":[OSD([subQ5,subQ1,subQ6,subQ7,subQ4,subQ3,subQ2,subQ0])],"isStart":false})})}),makeQuery(id+"F8.opExtrude","SWEPT_FACE",FACE,{"disambiguationData":[OSD([sQuery(id+"F7.wireOp",EDGE,"E67")])]})]});}
            var Q5;
            Q5=makeQuery(id+"F8.boolean.opBoolean","INTERSECT",EDGE,{"disambiguationData":[OD(0.0)],"derivedFrom":[makeQuery(id+"F5.opExtrude","SWEPT_FACE",FACE,{"disambiguationData":[OSD([sQuery(id+"F4.wireOp",EDGE,"E30")])]}),makeQuery(id+"F8.opExtrude","SWEPT_FACE",FACE,{"disambiguationData":[OSD([sQuery(id+"F7.wireOp",EDGE,"E67")])]})]});
            fillet(context, id + "F14", {"entities" : qUnion([Q0, Q1, Q2, Q3, Q4, Q5]), "radius" : 3 * mm, "tangentPropagation" : true, "allowEdgeOverflow" : false});
        }
        {
            var Q0;
            Q0=makeQuery(id+"F1.opExtrude","CAP_EDGE",EDGE,{"disambiguationData":[OSD([sQuery(id+"F0.wireOp",EDGE,"E1.bottom")])],"isStart":false});
            fillet(context, id + "F15", {"entities" : qUnion([Q0]), "radius" : 2 * mm, "tangentPropagation" : true, "allowEdgeOverflow" : false});
        }
        {
            var Q0;
            {var subQ0=sQuery(id+"F4.wireOp",EDGE,"E63.0.MirrorCS");var subQ1=sQuery(id+"F4.wireOp",EDGE,"E62.0.MirrorCS");var subQ2=sQuery(id+"F4.wireOp",EDGE,"E61.0.MirrorCS");var subQ3=sQuery(id+"F4.wireOp",EDGE,"E60.0.MirrorCS");var subQ4=sQuery(id+"F4.wireOp",EDGE,"E59.0.MirrorCS");var subQ5=sQuery(id+"F4.wireOp",EDGE,"E58.0.MirrorCS");var subQ6=sQuery(id+"F4.wireOp",EDGE,"E57.0.MirrorCS");var subQ7=sQuery(id+"F4.wireOp",EDGE,"E56.0.MirrorCS");var subQ8=sQuery(id+"F4.wireOp",EDGE,"E55.0.MirrorCS");var subQ9=sQuery(id+"F4.wireOp",EDGE,"E54.0.MirrorCS");var subQ10=sQuery(id+"F4.wireOp",EDGE,"E53.0.MirrorCS");var subQ11=sQuery(id+"F4.wireOp",EDGE,"E52.filletArc");var subQ12=sQuery(id+"F4.wireOp",EDGE,"E45");var subQ13=sQuery(id+"F4.wireOp",EDGE,"E43");var subQ14=sQuery(id+"F4.wireOp",EDGE,"E42");var subQ15=sQuery(id+"F4.wireOp",EDGE,"E41");var subQ16=sQuery(id+"F4.wireOp",EDGE,"E46");var subQ17=sQuery(id+"F4.wireOp",EDGE,"E47.filletArc");var subQ18=sQuery(id+"F4.wireOp",EDGE,"E48.filletArc");var subQ19=sQuery(id+"F4.wireOp",EDGE,"E49.filletArc");var subQ20=sQuery(id+"F4.wireOp",EDGE,"E50.filletArc");var subQ21=sQuery(id+"F4.wireOp",EDGE,"E51.filletArc");Q0=makeQuery(id+"F6.boolean.opBoolean","SPLIT",FACE,{"disambiguationData":[TD([makeQuery(id+"F5.opExtrude","SWEPT_FACE",FACE,{"disambiguationData":[OSD([subQ15])]})])],"derivedFrom":makeQuery(id+"F5.opExtrude","CAP_FACE",FACE,{"disambiguationData":[OSD([sQuery(id+"F4.wireOp",EDGE,"E27.0"),sQuery(id+"F4.wireOp",EDGE,"E28.0"),sQuery(id+"F4.wireOp",EDGE,"E29"),sQuery(id+"F4.wireOp",EDGE,"E30"),sQuery(id+"F4.wireOp",EDGE,"E33.filletArc"),sQuery(id+"F4.wireOp",EDGE,"E34.filletArc"),sQuery(id+"F4.wireOp",EDGE,"E35.filletArc"),sQuery(id+"F4.wireOp",EDGE,"E36.filletArc"),subQ15,subQ14,subQ13,subQ12,subQ16,subQ17,subQ18,subQ19,subQ20,subQ21,subQ11,subQ10,subQ9,subQ8,subQ7,subQ6,subQ5,subQ4,subQ3,subQ2,subQ1,subQ0])],"isStart":true})});}
            var sketch = newSketch(context, id + "F16", { "sketchPlane" : qUnion([Q0])});
            skSolve(sketch);
        }
        {
            var Q0;
            {var subQ0=sQuery(id+"F0.wireOp",EDGE,"E21.filletArc");var subQ1=sQuery(id+"F0.wireOp",EDGE,"E7");var subQ2=sQuery(id+"F0.wireOp",EDGE,"E6");var subQ3=sQuery(id+"F0.wireOp",EDGE,"E5");var subQ4=sQuery(id+"F0.wireOp",EDGE,"E4");var subQ5=sQuery(id+"F0.wireOp",EDGE,"E22.filletArc");var subQ6=sQuery(id+"F0.wireOp",EDGE,"E1.bottom");var subQ7=sQuery(id+"F0.wireOp",EDGE,"E1.right");var subQ8=sQuery(id+"F0.wireOp",EDGE,"E1.top");var subQ9=sQuery(id+"F0.wireOp",EDGE,"E1.left");var subQ10=sQuery(id+"F0.wireOp",EDGE,"E23.filletArc");var subQ11=sQuery(id+"F0.wireOp",EDGE,"E24.filletArc");Q0=makeQuery(id+"F2.boolean.opBoolean","SPLIT",FACE,{"disambiguationData":[TD([makeQuery(id+"F1.opExtrude","SWEPT_FACE",FACE,{"disambiguationData":[OSD([subQ6])]})])],"derivedFrom":makeQuery(id+"F1.opExtrude","CAP_FACE",FACE,{"disambiguationData":[OSD([subQ6,subQ8,subQ9,subQ7,subQ4,subQ3,subQ2,subQ1,subQ0,subQ5,subQ10,subQ11])],"isStart":true})});}
            var sketch = newSketch(context, id + "F17", { "sketchPlane" : qUnion([Q0])});
            skLineSegment(sketch, "E79", {"start": v(-41.36, 74.25) * mm, "end": v(-23.94, 92.25) * mm});
            skLineSegment(sketch, "E80", {"start": v(-23.94, 92.25) * mm, "end": v(-23.94, 100.18) * mm});
            skLineSegment(sketch, "E81", {"start": v(22.94, 74.25) * mm, "end": v(4.94, 92.25) * mm});
            skLineSegment(sketch, "E82", {"start": v(4.94, 92.25) * mm, "end": v(4.94, 100.18) * mm});
            skArc(sketch, "E83", {"start": v(4.94, 100.18) * mm, "mid": v(-9.5, 119.25) * mm, "end": v(-23.94, 100.18) * mm});
            skLineSegment(sketch, "E84", {"start": v(-9.5, 104.25) * mm, "end": v(-9.5, 74.25) * mm, "construction": true});
            skPoint(sketch, "E84.endSnap0", {"position": v(0, 74.25) * mm});
            skCircle(sketch, "E85", {"center": v(-9.5, 104.25) * mm, "radius": 6 * mm});
            skLineSegment(sketch, "E86", {"start": v(-74.25, 0) * mm, "end": v(74.25, 0) * mm, "construction": true});
            skLineSegment(sketch, "E87.MirrorCS", {"start": v(22.94, -74.25) * mm, "end": v(4.94, -92.25) * mm});
            skLineSegment(sketch, "E88.MirrorCS", {"start": v(4.94, -92.25) * mm, "end": v(4.94, -100.18) * mm});
            skArc(sketch, "E89.MirrorCS", {"start": v(4.94, -100.18) * mm, "mid": v(-9.5, -119.25) * mm, "end": v(-23.94, -100.18) * mm});
            skLineSegment(sketch, "E90.MirrorCS", {"start": v(-41.36, -74.25) * mm, "end": v(-23.94, -92.25) * mm});
            skCircle(sketch, "E91.MirrorC", {"center": v(-9.5, -104.25) * mm, "radius": 6 * mm});
            skLineSegment(sketch, "E92.MirrorCS", {"start": v(-23.94, -92.25) * mm, "end": v(-23.94, -100.18) * mm});
            skSolve(sketch);
        }
        {
            var Q0;
            {var subQ1=sQuery(id+"F17.wireOp",EDGE,"E79");Q0=makeQuery(id+"F17.imprint","IMPRINT",FACE,{"disambiguationData":[TD([[makeQuery(id+"F17.imprint","IMPRINT",EDGE,{"derivedFrom":subQ1}),-1.0]])]});}
            var Q1;
            Q1=makeQuery(id+"F17.imprint","IMPRINT",FACE,{"disambiguationData":[TD([[makeQuery(id+"F17.imprint","IMPRINT",EDGE,{"derivedFrom":makeQuery(id+"F1.opExtrude","CAP_EDGE",EDGE,{"disambiguationData":[OSD([sQuery(id+"F0.wireOp",EDGE,"E1.left")])],"isStart":true})}),-1.0]])]});
            var Q2;
            {var subQ1=sQuery(id+"F17.wireOp",EDGE,"E87.MirrorCS");Q2=makeQuery(id+"F17.imprint","IMPRINT",FACE,{"disambiguationData":[TD([[makeQuery(id+"F17.imprint","IMPRINT",EDGE,{"derivedFrom":subQ1}),-1.0]])]});}
            var Q3;
            Q3=makeQuery(id+"F2.opExtrude","CAP_FACE",FACE,{"disambiguationData":[OSD([sQuery(id+"F0.wireOp",EDGE,"E12"),sQuery(id+"F0.wireOp",EDGE,"E13"),sQuery(id+"F0.wireOp",EDGE,"E14"),sQuery(id+"F0.wireOp",EDGE,"E15"),sQuery(id+"F0.wireOp",EDGE,"E17.filletArc"),sQuery(id+"F0.wireOp",EDGE,"E18.filletArc"),sQuery(id+"F0.wireOp",EDGE,"E19.filletArc"),sQuery(id+"F0.wireOp",EDGE,"E20.filletArc"),sQuery(id+"F0.wireOp",EDGE,"E25.0"),sQuery(id+"F0.wireOp",EDGE,"E25.1"),sQuery(id+"F0.wireOp",EDGE,"E25.2"),sQuery(id+"F0.wireOp",EDGE,"E25.3"),sQuery(id+"F0.wireOp",EDGE,"E25.4"),sQuery(id+"F0.wireOp",EDGE,"E25.5"),sQuery(id+"F0.wireOp",EDGE,"E25.6"),sQuery(id+"F0.wireOp",EDGE,"E25.7")])],"isStart":false});
            extrude(context, id + "F18", {"entities" : qUnion([Q0, Q1, Q2]), "operationType" : NewBodyOperationType.ADD, "endBound" : BoundingType.UP_TO_SURFACE, "depth" : 25 * mm, "endBoundEntityFace" : qUnion([Q3]), "offsetDistance" : 25 * mm});
        }
    });
